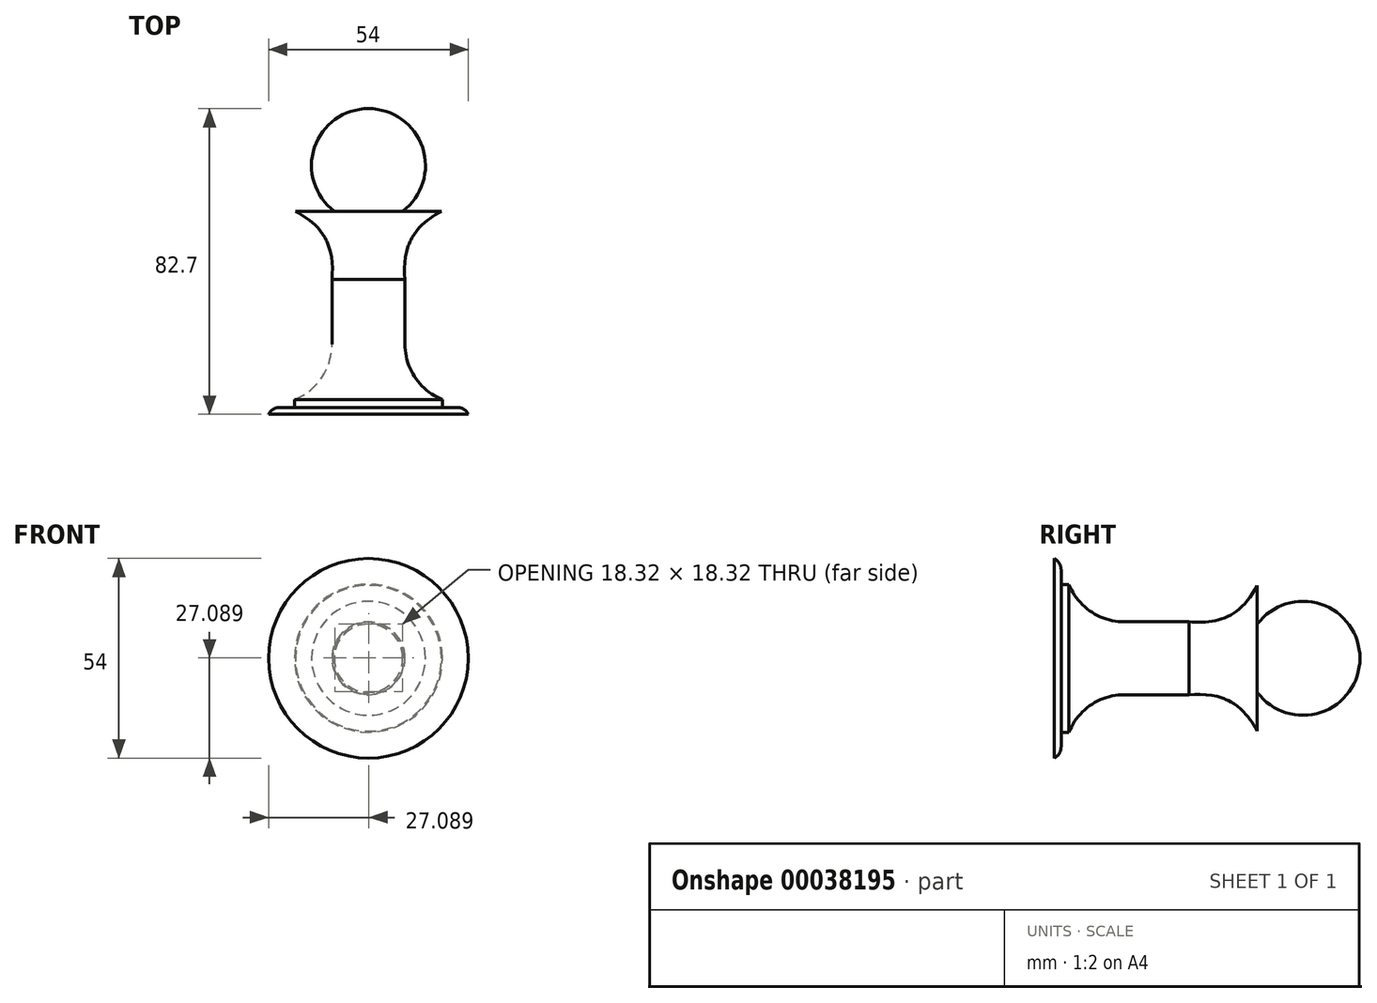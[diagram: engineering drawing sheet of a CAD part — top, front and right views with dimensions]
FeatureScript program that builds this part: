
annotation { "Feature Type Name" : "Feature", "Feature Type Description" : "" }
export const myFeature = defineFeature(function(context is Context, id is Id, definition is map)
    precondition{}
    {
        {
            var Q0;
            Q0=qCreatedBy(makeId("Top.planeOp"),FACE);
            var sketch = newSketch(context, id + "F0", { "sketchPlane" : qUnion([Q0])});
            skArc(sketch, "E0", {"start": v(9.25, -1.5) * mm, "mid": v(14.62, 15.7) * mm, "end": v(0, 26.24) * mm});
            skLineSegment(sketch, "E1", {"start": v(9.25, -1.5) * mm, "end": v(19.73, -1.5) * mm});
            skLineSegment(sketch, "E2", {"start": v(0, 10.83) * mm, "end": v(0, -1.5) * mm});
            skLineSegment(sketch, "E3", {"start": v(0, -1.5) * mm, "end": v(0, -20) * mm});
            skLineSegment(sketch, "E4", {"start": v(9.87, -20) * mm, "end": v(9.87, -37.46) * mm});
            skLineSegment(sketch, "E5", {"start": v(20, -54.57) * mm, "end": v(24, -54.57) * mm});
            skLineSegment(sketch, "E6", {"start": v(0, -56.46) * mm, "end": v(27, -56.46) * mm});
            skLineSegment(sketch, "E7", {"start": v(0, -37.46) * mm, "end": v(0, -52.46) * mm});
            skLineSegment(sketch, "E8", {"start": v(0, -52.46) * mm, "end": v(0, -56.46) * mm});
            skFitSpline(sketch, "E9", {"points": [v(19.73, -1.5) * mm, v(9.87, -20) * mm], "startDerivative": vector(-27.65, -14.67) * mm, "endDerivative": vector(1.56, -21.3) * mm});
            skArc(sketch, "E10", {"start": v(9.87, -37.46) * mm, "mid": v(12.64, -46.5) * mm, "end": v(20, -52.46) * mm});
            skArc(sketch, "E11", {"start": v(27, -56.46) * mm, "mid": v(25.77, -55.08) * mm, "end": v(24, -54.57) * mm});
            skLineSegment(sketch, "E12", {"start": v(0, 26.24) * mm, "end": v(0, -4.59) * mm});
            skLineSegment(sketch, "E13", {"start": v(20, -52.46) * mm, "end": v(20, -54.57) * mm});
            skLineSegment(sketch, "E14", {"start": v(0, -20) * mm, "end": v(0, -37.46) * mm});
            skSolve(sketch);
        }
        {
            var Q0;
            {var subQ2=sQuery(id+"F0.wireOp",EDGE,"E0");Q0=makeQuery(id+"F0.imprint","IMPRINT",FACE,{"disambiguationData":[TD([[makeQuery(id+"F0.imprint","IMPRINT",EDGE,{"derivedFrom":subQ2}),1.0]])]});}
            var Q1;
            Q1=sQuery(id+"F0.wireOp",EDGE,"E12");
            revolve(context, id + "F1", {"entities" : qUnion([Q0]), "axis" : qUnion([Q1]), "revolveType" : RevolveType.FULL});
        }
    });
